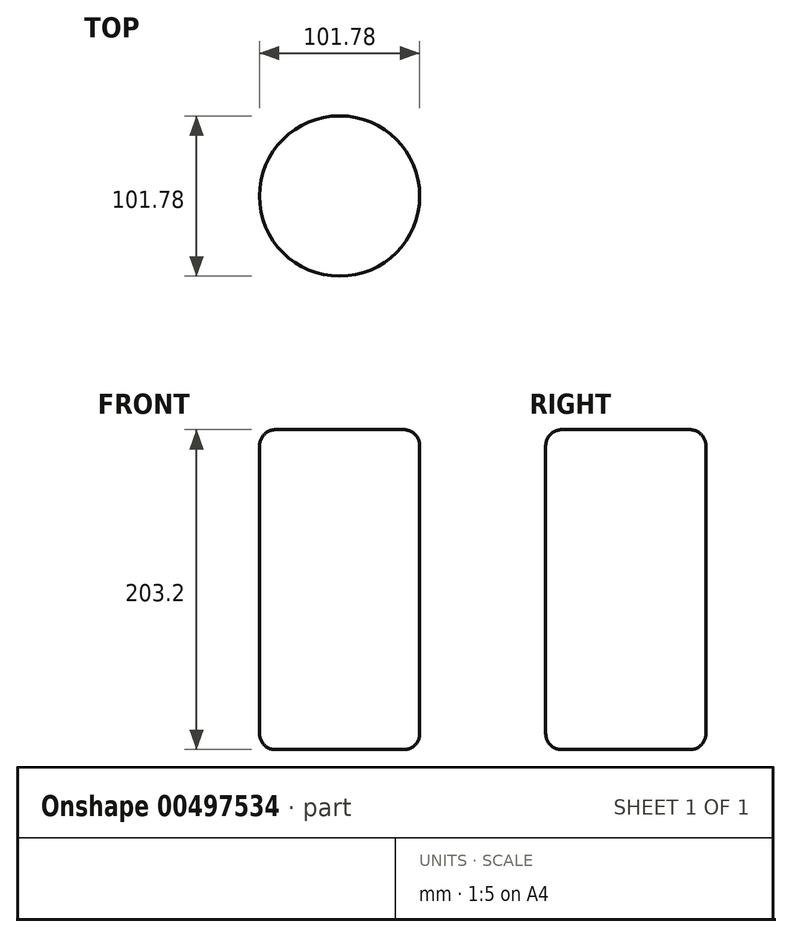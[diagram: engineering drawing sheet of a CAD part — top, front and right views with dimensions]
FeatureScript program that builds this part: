
annotation { "Feature Type Name" : "Feature", "Feature Type Description" : "" }
export const myFeature = defineFeature(function(context is Context, id is Id, definition is map)
    precondition{}
    {
        {
            var Q0;
            Q0=qCreatedBy(makeId("Top.planeOp"),FACE);
            var sketch = newSketch(context, id + "F0", { "sketchPlane" : qUnion([Q0])});
            skCircle(sketch, "E0", {"center": v(0, 0) * mm, "radius": 50.9 * mm});
            skSolve(sketch);
        }
        {
            var Q0;
            Q0 = qSketchRegion(id + "F0", true);
            extrude(context, id + "F1", {"entities" : qUnion([Q0]), "depth" : 203.2 * mm});
        }
        {
            var Q0;
            Q0=makeQuery(id+"F1.opExtrude","CAP_FACE",FACE,{"disambiguationData":[OSD([sQuery(id+"F0.wireOp",EDGE,"E0")])],"isStart":true});
            var Q1;
            Q1=makeQuery(id+"F1.opExtrude","CAP_EDGE",EDGE,{"disambiguationData":[OSD([sQuery(id+"F0.wireOp",EDGE,"E0")])],"isStart":true});
            fillet(context, id + "F2", {"entities" : qUnion([Q0, Q1]), "radius" : 10.16 * mm, "tangentPropagation" : true, "allowEdgeOverflow" : false});
        }
        {
            var Q0;
            Q0=makeQuery(id+"F1.opExtrude","CAP_FACE",FACE,{"disambiguationData":[OSD([sQuery(id+"F0.wireOp",EDGE,"E0")])],"isStart":false});
            fillet(context, id + "F3", {"entities" : qUnion([Q0]), "radius" : 10.16 * mm, "tangentPropagation" : true, "allowEdgeOverflow" : false});
        }
    });
